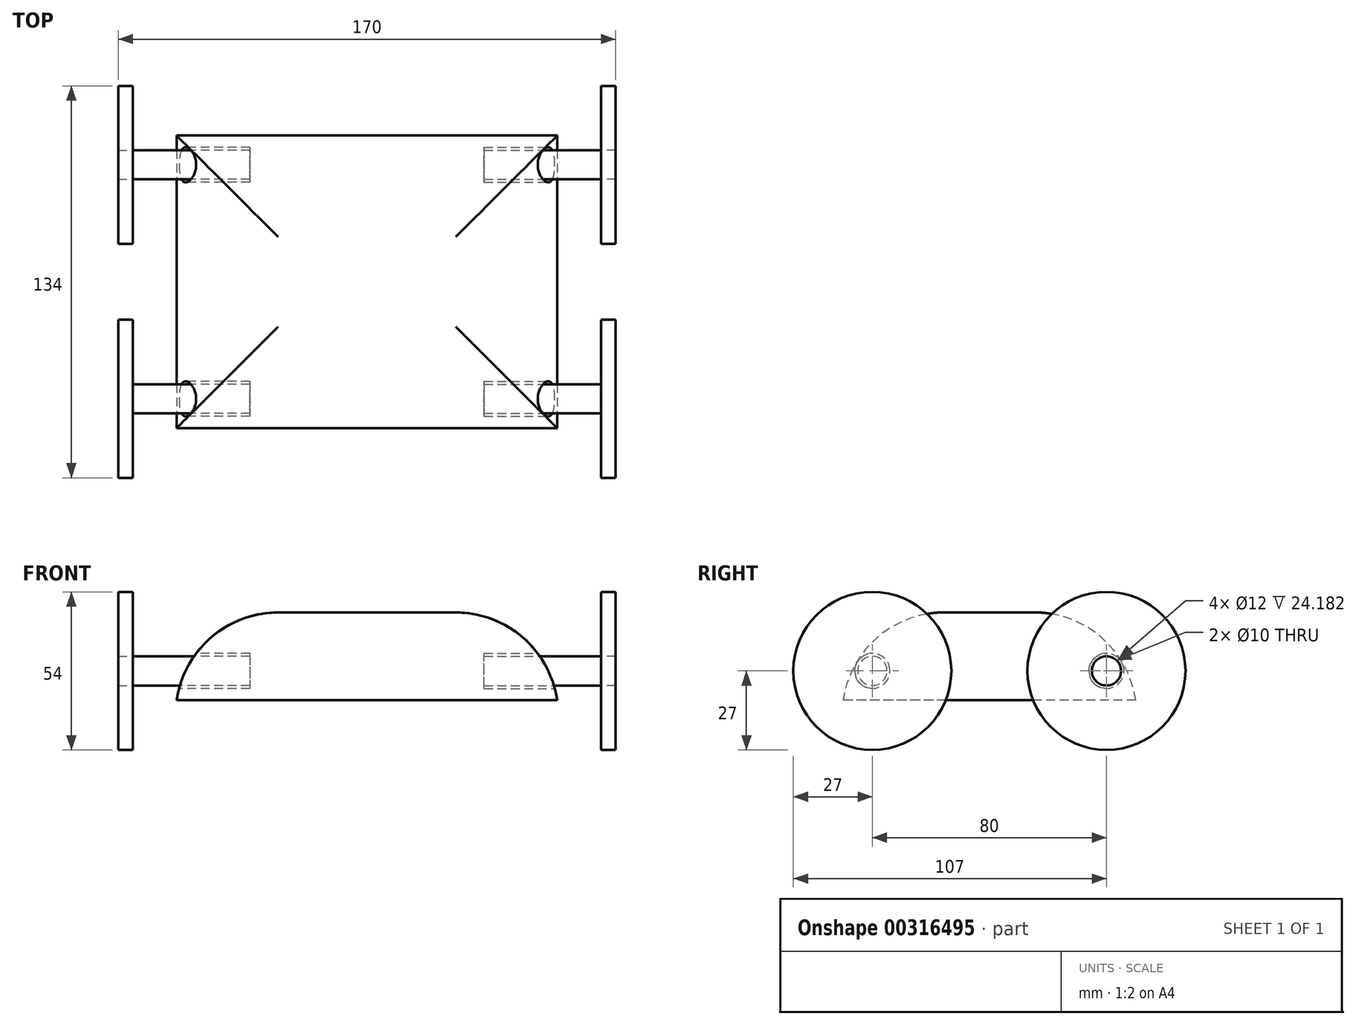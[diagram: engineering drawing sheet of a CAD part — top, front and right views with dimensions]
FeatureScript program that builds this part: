
annotation { "Feature Type Name" : "Feature", "Feature Type Description" : "" }
export const myFeature = defineFeature(function(context is Context, id is Id, definition is map)
    precondition{}
    {
        {
            var Q0;
            Q0=qCreatedBy(makeId("Top.planeOp"),FACE);
            var sketch = newSketch(context, id + "F0", { "sketchPlane" : qUnion([Q0])});
            skLineSegment(sketch, "E0.bottom", {"start": v(-65, 50) * mm, "end": v(65, 50) * mm});
            skLineSegment(sketch, "E0.top", {"start": v(-65, -50) * mm, "end": v(65, -50) * mm});
            skLineSegment(sketch, "E0.left", {"start": v(-65, 50) * mm, "end": v(-65, -50) * mm});
            skLineSegment(sketch, "E0.right", {"start": v(65, 50) * mm, "end": v(65, -50) * mm});
            skPoint(sketch, "E0.middle", {"position": v(0, 0) * mm});
            skSolve(sketch);
        }
        {
            var Q0;
            Q0=makeQuery(id+"F0.imprint","IMPRINT",FACE,{"disambiguationData":[TD([[makeQuery(id+"F0.imprint","IMPRINT",EDGE,{"derivedFrom":sQuery(id+"F0.wireOp",EDGE,"E0.bottom")}),-1.0]])]});
            extrude(context, id + "F1", {"entities" : qUnion([Q0]), "depth" : 20 * mm});
        }
        {
            var Q0;
            Q0=makeQuery(id+"F1.opExtrude","CAP_FACE",FACE,{"disambiguationData":[OSD([sQuery(id+"F0.wireOp",EDGE,"E0.bottom"),sQuery(id+"F0.wireOp",EDGE,"E0.top"),sQuery(id+"F0.wireOp",EDGE,"E0.left"),sQuery(id+"F0.wireOp",EDGE,"E0.right")])],"isStart":true});
            extrude(context, id + "F2", {"entities" : qUnion([Q0]), "operationType" : NewBodyOperationType.ADD, "depth" : 10 * mm});
        }
        {
            var Q0;
            {var subQ0=sQuery(id+"F0.wireOp",EDGE,"E0.left");Q0=makeQuery(id+"F2.boolean.opBoolean","MERGE",FACE,{"derivedFrom":[makeQuery(id+"F1.opExtrude","SWEPT_FACE",FACE,{"disambiguationData":[OSD([subQ0])]}),makeQuery(id+"F2.opExtrude","SWEPT_FACE",FACE,{"disambiguationData":[OSD([subQ0])]})]});}
            var sketch = newSketch(context, id + "F3", { "sketchPlane" : qUnion([Q0])});
            skCircle(sketch, "E1", {"center": v(-40, 0) * mm, "radius": 6 * mm});
            skLineSegment(sketch, "E2", {"start": v(-40, 0) * mm, "end": v(0, 0) * mm});
            skLineSegment(sketch, "E3", {"start": v(0, 0) * mm, "end": v(40, 0) * mm});
            skCircle(sketch, "E4", {"center": v(40, 0) * mm, "radius": 6 * mm});
            skCircle(sketch, "E5", {"center": v(-40, 0) * mm, "radius": 5 * mm});
            skCircle(sketch, "E6", {"center": v(40, 0) * mm, "radius": 5 * mm});
            skSolve(sketch);
        }
        {
            var Q0;
            Q0=makeQuery(id+"F3.imprint","IMPRINT",FACE,{"disambiguationData":[TD([[makeQuery(id+"F3.imprint","IMPRINT",EDGE,{"derivedFrom":sQuery(id+"F3.wireOp",EDGE,"E1")}),1.0]])]});
            extrude(context, id + "F4", {"entities" : qUnion([Q0]), "operationType" : NewBodyOperationType.REMOVE, "depth" : -25 * mm});
        }
        {
            var Q0;
            {var subQ0=sQuery(id+"F0.wireOp",EDGE,"E0.left");Q0=makeQuery(id+"F4.boolean.opBoolean","SPLIT",FACE,{"disambiguationData":[TD([makeQuery(id+"F4.opExtrude","SWEPT_FACE",FACE,{"disambiguationData":[OSD([sQuery(id+"F3.wireOp",EDGE,"E5")])]})])],"derivedFrom":makeQuery(id+"F2.boolean.opBoolean","MERGE",FACE,{"derivedFrom":[makeQuery(id+"F1.opExtrude","SWEPT_FACE",FACE,{"disambiguationData":[OSD([subQ0])]}),makeQuery(id+"F2.opExtrude","SWEPT_FACE",FACE,{"disambiguationData":[OSD([subQ0])]})]})});}
            extrude(context, id + "F5", {"entities" : qUnion([Q0]), "operationType" : NewBodyOperationType.ADD, "depth" : 15 * mm});
        }
        {
            var Q0;
            Q0=makeQuery(id+"F3.imprint","IMPRINT",FACE,{"disambiguationData":[TD([[makeQuery(id+"F3.imprint","IMPRINT",EDGE,{"derivedFrom":sQuery(id+"F3.wireOp",EDGE,"E4")}),1.0]])]});
            extrude(context, id + "F6", {"entities" : qUnion([Q0]), "operationType" : NewBodyOperationType.REMOVE, "oppositeDirection" : true, "depth" : 25 * mm});
        }
        {
            var Q0;
            {var subQ0=sQuery(id+"F0.wireOp",EDGE,"E0.bottom");var subQ3=sQuery(id+"F0.wireOp",EDGE,"E0.left");Q0=makeQuery(id+"F6.boolean.opBoolean","SPLIT",FACE,{"disambiguationData":[TD([makeQuery(id+"F6.opExtrude","SWEPT_FACE",FACE,{"disambiguationData":[OSD([sQuery(id+"F3.wireOp",EDGE,"E6")])]})])],"derivedFrom":makeQuery(id+"F4.boolean.opBoolean","SPLIT",FACE,{"disambiguationData":[TD([makeQuery(id+"F1.opExtrude","SWEPT_FACE",FACE,{"disambiguationData":[OSD([subQ0])]})])],"derivedFrom":makeQuery(id+"F2.boolean.opBoolean","MERGE",FACE,{"derivedFrom":[makeQuery(id+"F1.opExtrude","SWEPT_FACE",FACE,{"disambiguationData":[OSD([subQ3])]}),makeQuery(id+"F2.opExtrude","SWEPT_FACE",FACE,{"disambiguationData":[OSD([subQ3])]})]})})});}
            extrude(context, id + "F7", {"entities" : qUnion([Q0]), "operationType" : NewBodyOperationType.ADD, "depth" : 15 * mm});
        }
        {
            var Q0;
            {var subQ0=sQuery(id+"F0.wireOp",EDGE,"E0.right");Q0=makeQuery(id+"F2.boolean.opBoolean","MERGE",FACE,{"derivedFrom":[makeQuery(id+"F1.opExtrude","SWEPT_FACE",FACE,{"disambiguationData":[OSD([subQ0])]}),makeQuery(id+"F2.opExtrude","SWEPT_FACE",FACE,{"disambiguationData":[OSD([subQ0])]})]});}
            var sketch = newSketch(context, id + "F8", { "sketchPlane" : qUnion([Q0])});
            skLineSegment(sketch, "E7", {"start": v(0, 0) * mm, "end": v(-40, 0) * mm});
            skLineSegment(sketch, "E8", {"start": v(0, 0) * mm, "end": v(40, 0) * mm});
            skCircle(sketch, "E9", {"center": v(-40, 0) * mm, "radius": 6 * mm});
            skCircle(sketch, "E10", {"center": v(-40, 0) * mm, "radius": 5 * mm});
            skCircle(sketch, "E11", {"center": v(40, 0) * mm, "radius": 5 * mm});
            skCircle(sketch, "E12", {"center": v(40, 0) * mm, "radius": 6 * mm});
            skSolve(sketch);
        }
        {
            var Q0;
            Q0=makeQuery(id+"F8.imprint","IMPRINT",FACE,{"disambiguationData":[TD([[makeQuery(id+"F8.imprint","IMPRINT",EDGE,{"derivedFrom":sQuery(id+"F8.wireOp",EDGE,"E9")}),1.0]])]});
            var Q1;
            Q1=makeQuery(id+"F8.imprint","IMPRINT",FACE,{"disambiguationData":[TD([[makeQuery(id+"F8.imprint","IMPRINT",EDGE,{"derivedFrom":sQuery(id+"F8.wireOp",EDGE,"E11")}),-1.0]])]});
            extrude(context, id + "F9", {"entities" : qUnion([Q0, Q1]), "operationType" : NewBodyOperationType.REMOVE, "oppositeDirection" : true, "depth" : 25 * mm});
        }
        {
            var Q0;
            {var subQ0=sQuery(id+"F0.wireOp",EDGE,"E0.right");Q0=makeQuery(id+"F9.boolean.opBoolean","SPLIT",FACE,{"disambiguationData":[TD([makeQuery(id+"F9.opExtrude","SWEPT_FACE",FACE,{"disambiguationData":[OSD([sQuery(id+"F8.wireOp",EDGE,"E10")])]})])],"derivedFrom":makeQuery(id+"F2.boolean.opBoolean","MERGE",FACE,{"derivedFrom":[makeQuery(id+"F1.opExtrude","SWEPT_FACE",FACE,{"disambiguationData":[OSD([subQ0])]}),makeQuery(id+"F2.opExtrude","SWEPT_FACE",FACE,{"disambiguationData":[OSD([subQ0])]})]})});}
            var Q1;
            {var subQ0=sQuery(id+"F0.wireOp",EDGE,"E0.right");Q1=makeQuery(id+"F9.boolean.opBoolean","SPLIT",FACE,{"disambiguationData":[TD([makeQuery(id+"F9.opExtrude","SWEPT_FACE",FACE,{"disambiguationData":[OSD([sQuery(id+"F8.wireOp",EDGE,"E11")])]})])],"derivedFrom":makeQuery(id+"F2.boolean.opBoolean","MERGE",FACE,{"derivedFrom":[makeQuery(id+"F1.opExtrude","SWEPT_FACE",FACE,{"disambiguationData":[OSD([subQ0])]}),makeQuery(id+"F2.opExtrude","SWEPT_FACE",FACE,{"disambiguationData":[OSD([subQ0])]})]})});}
            extrude(context, id + "F10", {"entities" : qUnion([Q0, Q1]), "operationType" : NewBodyOperationType.ADD, "depth" : 15 * mm});
        }
        {
            var Q0;
            Q0=makeQuery(id+"F5.opExtrude","CAP_FACE",FACE,{"disambiguationData":[OSD([sQuery(id+"F0.wireOp",EDGE,"E0.left")])],"isStart":false});
            var sketch = newSketch(context, id + "F11", { "sketchPlane" : qUnion([Q0])});
            skCircle(sketch, "E13", {"center": v(-40, 0) * mm, "radius": 27 * mm});
            skSolve(sketch);
        }
        {
            var Q0;
            Q0=makeQuery(id+"F7.opExtrude","CAP_FACE",FACE,{"disambiguationData":[OSD([sQuery(id+"F0.wireOp",EDGE,"E0.left")])],"isStart":false});
            var sketch = newSketch(context, id + "F12", { "sketchPlane" : qUnion([Q0])});
            skCircle(sketch, "E14", {"center": v(40, 0) * mm, "radius": 27 * mm});
            skSolve(sketch);
        }
        {
            var Q0;
            Q0=makeQuery(id+"F12.imprint","IMPRINT",FACE,{"disambiguationData":[TD([[makeQuery(id+"F12.imprint","IMPRINT",EDGE,{"derivedFrom":sQuery(id+"F12.wireOp",EDGE,"E14")}),1.0]])]});
            var Q1;
            Q1=makeQuery(id+"F12.imprint","IMPRINT",FACE,{"disambiguationData":[TD([[makeQuery(id+"F12.imprint","IMPRINT",EDGE,{"derivedFrom":makeQuery(id+"F7.opExtrude","CAP_EDGE",EDGE,{"disambiguationData":[OSD([sQuery(id+"F3.wireOp",EDGE,"E6")])],"isStart":false})}),1.0]])]});
            extrude(context, id + "F13", {"entities" : qUnion([Q0, Q1]), "operationType" : NewBodyOperationType.ADD, "depth" : 5 * mm});
        }
        {
            var Q0;
            {var subQ0=sQuery(id+"F0.wireOp",EDGE,"E0.right");Q0=makeQuery(id+"F10.opExtrude","CAP_FACE",FACE,{"disambiguationData":[OSD([subQ0]),TDD([makeQuery(id+"F9.boolean.opBoolean","SPLIT",FACE,{"disambiguationData":[TD([makeQuery(id+"F9.opExtrude","SWEPT_FACE",FACE,{"disambiguationData":[OSD([sQuery(id+"F8.wireOp",EDGE,"E10")])]})])],"derivedFrom":makeQuery(id+"F2.boolean.opBoolean","MERGE",FACE,{"derivedFrom":[makeQuery(id+"F1.opExtrude","SWEPT_FACE",FACE,{"disambiguationData":[OSD([subQ0])]}),makeQuery(id+"F2.opExtrude","SWEPT_FACE",FACE,{"disambiguationData":[OSD([subQ0])]})]})})])],"isStart":false});}
            var sketch = newSketch(context, id + "F14", { "sketchPlane" : qUnion([Q0])});
            skCircle(sketch, "E15", {"center": v(-40, 0) * mm, "radius": 27 * mm});
            skSolve(sketch);
        }
        {
            var Q0;
            Q0 = qSketchRegion(id + "F14", true);
            extrude(context, id + "F15", {"entities" : qUnion([Q0]), "operationType" : NewBodyOperationType.ADD, "depth" : 5 * mm});
        }
        {
            var Q0;
            {var subQ0=sQuery(id+"F0.wireOp",EDGE,"E0.right");Q0=makeQuery(id+"F10.opExtrude","CAP_FACE",FACE,{"disambiguationData":[OSD([subQ0]),TDD([makeQuery(id+"F9.boolean.opBoolean","SPLIT",FACE,{"disambiguationData":[TD([makeQuery(id+"F9.opExtrude","SWEPT_FACE",FACE,{"disambiguationData":[OSD([sQuery(id+"F8.wireOp",EDGE,"E11")])]})])],"derivedFrom":makeQuery(id+"F2.boolean.opBoolean","MERGE",FACE,{"derivedFrom":[makeQuery(id+"F1.opExtrude","SWEPT_FACE",FACE,{"disambiguationData":[OSD([subQ0])]}),makeQuery(id+"F2.opExtrude","SWEPT_FACE",FACE,{"disambiguationData":[OSD([subQ0])]})]})})])],"isStart":false});}
            var sketch = newSketch(context, id + "F16", { "sketchPlane" : qUnion([Q0])});
            skCircle(sketch, "E16", {"center": v(40, 0) * mm, "radius": 27 * mm});
            skSolve(sketch);
        }
        {
            var Q0;
            Q0=makeQuery(id+"F16.imprint","IMPRINT",FACE,{"disambiguationData":[TD([[makeQuery(id+"F16.imprint","IMPRINT",EDGE,{"derivedFrom":sQuery(id+"F16.wireOp",EDGE,"E16")}),1.0]])]});
            extrude(context, id + "F17", {"entities" : qUnion([Q0]), "depth" : 5 * mm});
        }
        {
            var Q0;
            Q0=makeQuery(id+"F11.imprint","IMPRINT",FACE,{"disambiguationData":[TD([[makeQuery(id+"F11.imprint","IMPRINT",EDGE,{"derivedFrom":sQuery(id+"F11.wireOp",EDGE,"E13")}),1.0]])]});
            extrude(context, id + "F18", {"entities" : qUnion([Q0]), "depth" : 5 * mm});
        }
        {
            var Q0;
            Q0=makeQuery(id+"F1.opExtrude","CAP_EDGE",EDGE,{"disambiguationData":[OSD([sQuery(id+"F0.wireOp",EDGE,"E0.bottom")])],"isStart":false});
            var Q1;
            Q1=makeQuery(id+"F1.opExtrude","CAP_EDGE",EDGE,{"disambiguationData":[OSD([sQuery(id+"F0.wireOp",EDGE,"E0.left")])],"isStart":false});
            var Q2;
            Q2=makeQuery(id+"F1.opExtrude","CAP_EDGE",EDGE,{"disambiguationData":[OSD([sQuery(id+"F0.wireOp",EDGE,"E0.top")])],"isStart":false});
            var Q3;
            Q3=makeQuery(id+"F1.opExtrude","CAP_EDGE",EDGE,{"disambiguationData":[OSD([sQuery(id+"F0.wireOp",EDGE,"E0.right")])],"isStart":false});
            fillet(context, id + "F19", {"entities" : qUnion([Q0, Q1, Q2, Q3]), "radius" : 35 * mm, "tangentPropagation" : true, "allowEdgeOverflow" : false});
        }
    });
